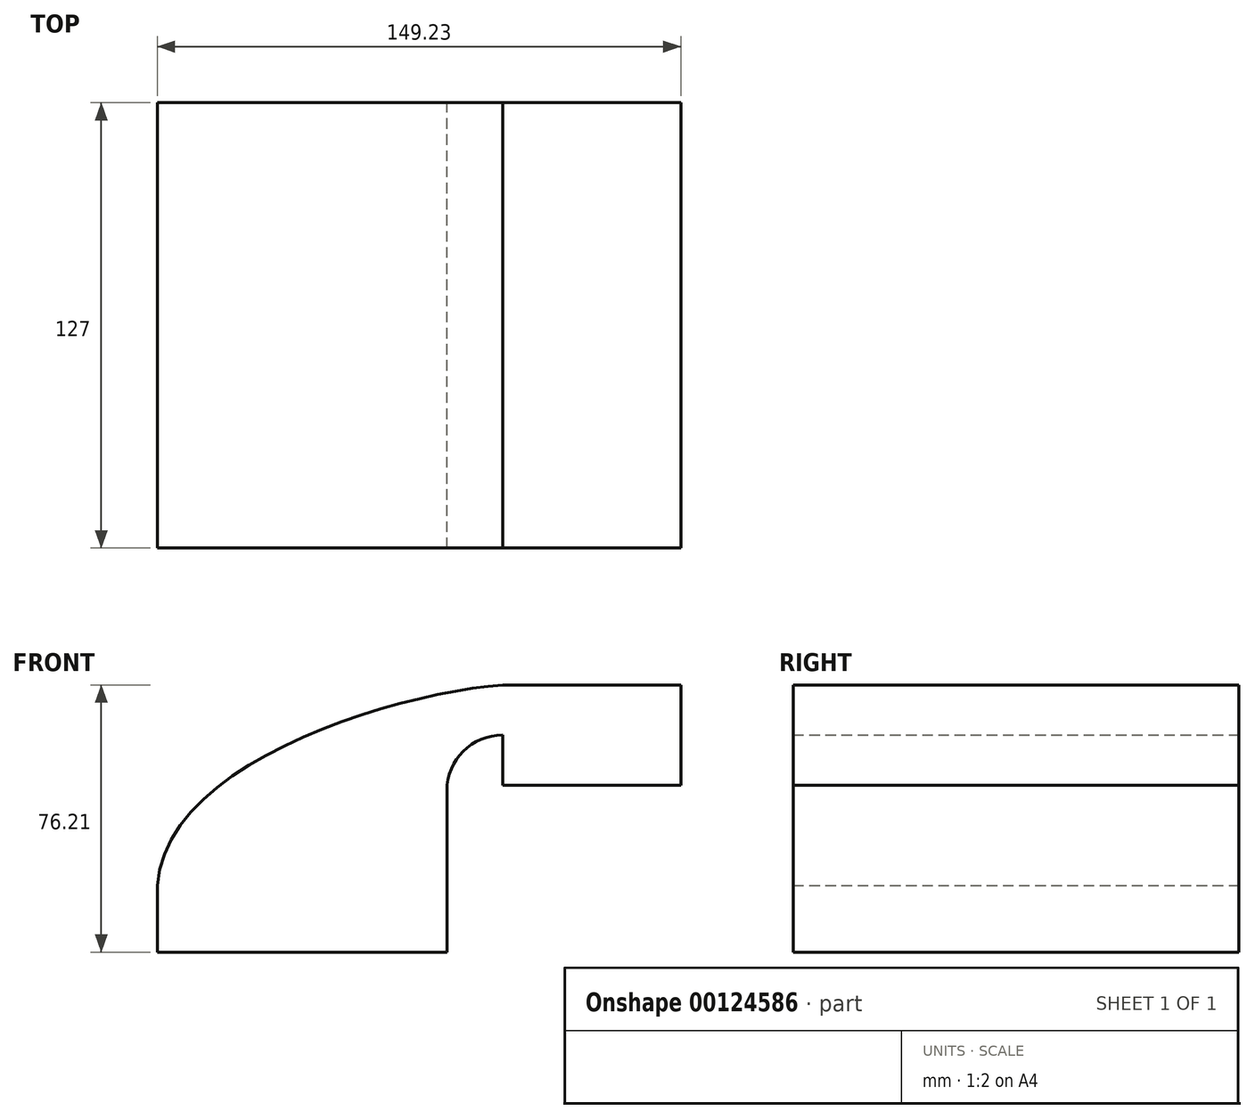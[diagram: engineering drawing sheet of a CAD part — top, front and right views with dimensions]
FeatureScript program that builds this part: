
annotation { "Feature Type Name" : "Feature", "Feature Type Description" : "" }
export const myFeature = defineFeature(function(context is Context, id is Id, definition is map)
    precondition{}
    {
        {
            var Q0;
            Q0=qCreatedBy(makeId("Front.planeOp"),FACE);
            var sketch = newSketch(context, id + "F0", { "sketchPlane" : qUnion([Q0])});
            skLineSegment(sketch, "E0.bottom", {"start": v(-41.28, 9.53) * mm, "end": v(41.28, 9.53) * mm});
            skLineSegment(sketch, "E0.top", {"start": v(-41.28, -9.53) * mm, "end": v(41.28, -9.53) * mm});
            skLineSegment(sketch, "E0.left", {"start": v(-41.28, 9.53) * mm, "end": v(-41.28, -9.53) * mm});
            skLineSegment(sketch, "E0.right", {"start": v(41.28, 9.53) * mm, "end": v(41.28, -9.53) * mm});
            skPoint(sketch, "E0.middle", {"position": v(0, 0) * mm});
            skLineSegment(sketch, "E1.bottom", {"start": v(57.15, 38.1) * mm, "end": v(107.95, 38.1) * mm});
            skLineSegment(sketch, "E1.top", {"start": v(57.15, 66.67) * mm, "end": v(107.95, 66.67) * mm});
            skLineSegment(sketch, "E1.left", {"start": v(57.15, 38.1) * mm, "end": v(57.15, 66.67) * mm});
            skLineSegment(sketch, "E1.right", {"start": v(107.95, 38.1) * mm, "end": v(107.95, 66.68) * mm});
            skPoint(sketch, "E1.middle", {"position": v(82.55, 52.39) * mm});
            skLineSegment(sketch, "E2", {"start": v(41.28, 9.53) * mm, "end": v(41.28, 36.51) * mm});
            skArc(sketch, "E3", {"start": v(41.28, 36.51) * mm, "mid": v(45.92, 47.74) * mm, "end": v(57.15, 52.39) * mm});
            skLineSegment(sketch, "E4", {"start": v(57.15, 52.39) * mm, "end": v(82.55, 52.39) * mm});
            skLineSegment(sketch, "E5.0", {"start": v(57.15, 66.36) * mm, "end": v(82.55, 66.36) * mm});
            skArc(sketch, "E5.1", {"start": v(27.3, 36.51) * mm, "mid": v(36.05, 57.62) * mm, "end": v(57.15, 66.36) * mm});
            skLineSegment(sketch, "E5.2", {"start": v(27.3, -0.64) * mm, "end": v(27.3, 36.51) * mm});
            skLineSegment(sketch, "E6", {"start": v(82.55, 52.39) * mm, "end": v(82.55, 66.36) * mm});
            skFitSpline(sketch, "E7", {"points": [v(-41.28, 9.53) * mm, v(57.15, 66.67) * mm], "startDerivative": vector(7.63, 106.5) * mm, "endDerivative": vector(90.67, 7.07) * mm});
            skSolve(sketch);
        }
        {
            var Q0;
            Q0 = qSketchRegion(id + "F0", true);
            extrude(context, id + "F1", {"entities" : qUnion([Q0]), "endBound" : BoundingType.SYMMETRIC, "depth" : 127 * mm});
        }
    });
